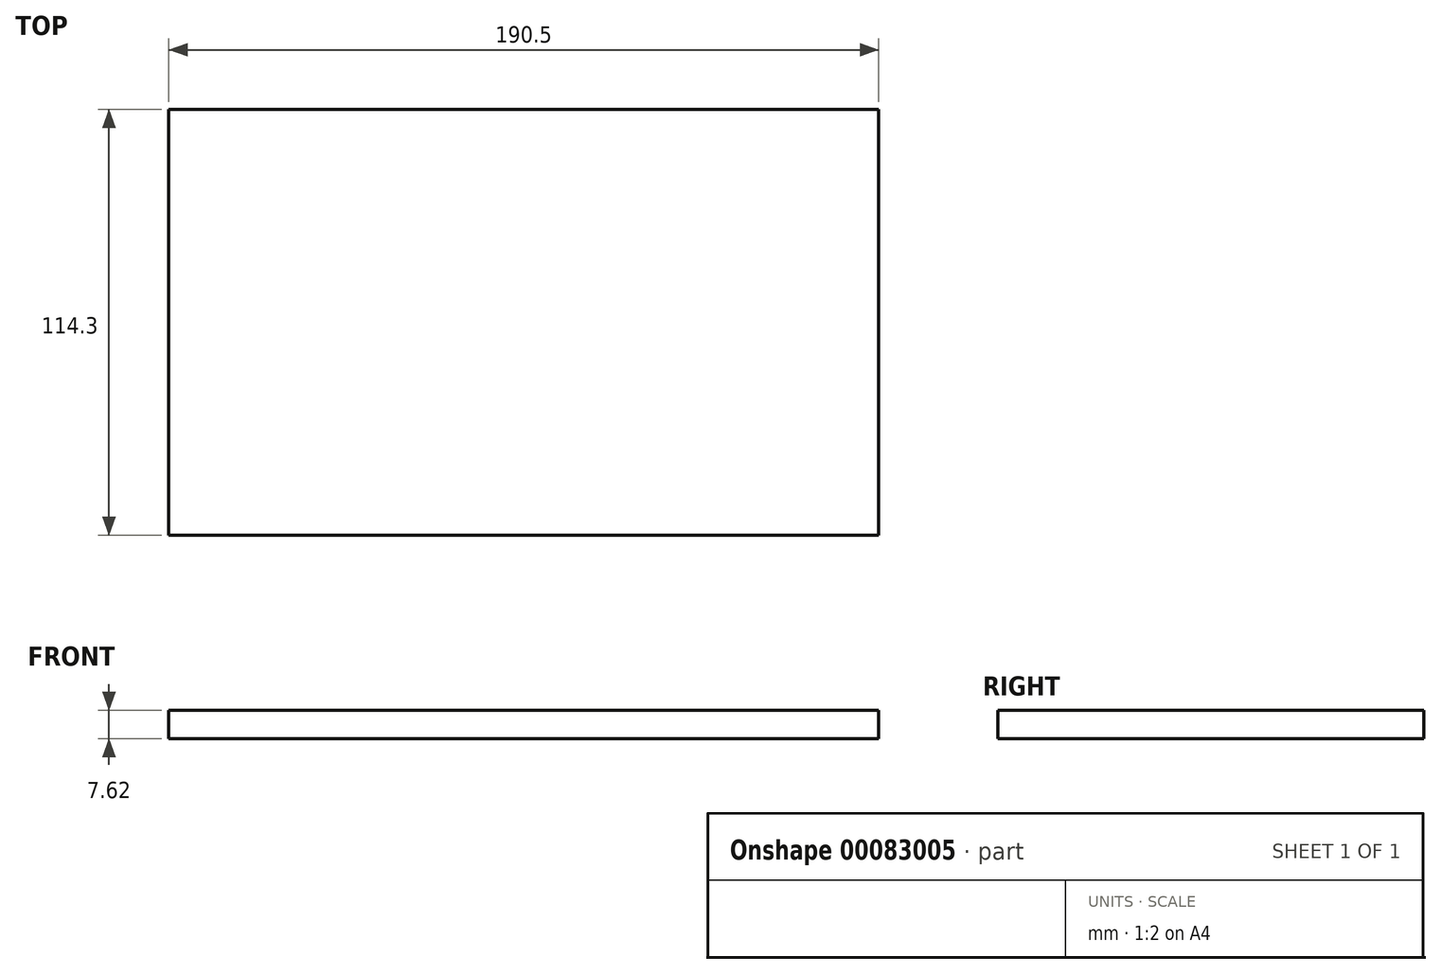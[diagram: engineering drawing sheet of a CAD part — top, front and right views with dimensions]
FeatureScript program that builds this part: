
annotation { "Feature Type Name" : "Feature", "Feature Type Description" : "" }
export const myFeature = defineFeature(function(context is Context, id is Id, definition is map)
    precondition{}
    {
        {
            var Q0;
            Q0=qCreatedBy(makeId("Top.planeOp"),FACE);
            var sketch = newSketch(context, id + "F0", { "sketchPlane" : qUnion([Q0])});
            skLineSegment(sketch, "E0.bottom", {"start": v(-240.15, 128.96) * mm, "end": v(-49.65, 128.96) * mm});
            skLineSegment(sketch, "E0.top", {"start": v(-240.15, 14.66) * mm, "end": v(-49.65, 14.66) * mm});
            skLineSegment(sketch, "E0.left", {"start": v(-240.15, 128.96) * mm, "end": v(-240.15, 14.66) * mm});
            skLineSegment(sketch, "E0.right", {"start": v(-49.65, 128.96) * mm, "end": v(-49.65, 14.66) * mm});
            skSolve(sketch);
        }
        {
            var Q0;
            Q0=makeQuery(id+"F0.imprint","IMPRINT",FACE,{"disambiguationData":[TD([[makeQuery(id+"F0.imprint","IMPRINT",EDGE,{"derivedFrom":sQuery(id+"F0.wireOp",EDGE,"E0.bottom")}),-1.0]])]});
            extrude(context, id + "F1", {"entities" : qUnion([Q0]), "depth" : 7.62 * mm});
        }
    });
